FCSTD DOCUMENT  (FreeCAD 1.0R39319 (Git))
Label: Assy_Simulator_Mockup
License: All rights reserved
LicenseURL: https://en.wikipedia.org/wiki/All_rights_reserved
objects: App::AnnotationLabel×5, App::DocumentObjectGroup×4, App::Link×3, PartDesign::CoordinateSystem×1, App::FeaturePython×1, App::Part×1
note: 1 computed .brp shape members not serialized (recipe doc carries the construction recipe); baked Part::Feature solids carry a one-line shape summary decoded from their .brp
EXTERNAL_REF file=../../Part/Misc/Floor.FCStd obj=reference_point
EXTERNAL_REF file=../../Part/Misc/Floor.FCStd obj=Part
EXTERNAL_REF file=Assy_PiTrac.FCStd obj=LCS_Origin
EXTERNAL_REF file=Assy_PiTrac.FCStd obj=Assembly
EXTERNAL_REF file=Assy_Calibration_Rig.FCStd obj=LCS_Origin
EXTERNAL_REF file=Assy_Calibration_Rig.FCStd obj=Assembly

FEATURE [App::DocumentObjectGroup] Parts
FEATURE [PartDesign::CoordinateSystem] LCS_Origin
  AttacherType = Attacher::AttachEngine3D
  AttachmentSupport = -> [X_Axis]
  MapMode = 2
FEATURE [App::DocumentObjectGroup] Constraints
FEATURE [App::FeaturePython] Variables  # WARN: FeaturePython — macro-defined, semantics opaque (R4)
  Type = App::PropertyContainer
FEATURE [App::DocumentObjectGroup] Configurations
FEATURE [App::Link] Floor
  AttachedBy = #reference_point
  AttachedTo = Parent Assembly#LCS_Origin
  LinkedObject = -> <external ../../Part/Misc/Floor.FCStd>#Part
  SolverId = Asm4EE
  expr: Placement = LCS_Origin.Placement * AttachmentOffset * Floor#reference_point.Placement ^ -1
FEATURE [App::Link] Assy_PiTrac
  AttachedBy = #LCS_Origin
  AttachedTo = Floor#reference_point
  AttachmentOffset = pos=(-66.5,5,16.5) rot=(0,0,1;0rad)
  LinkPlacement = pos=(-66.5,5,16.5) rot=(0,0,1;0rad)
  LinkedObject = -> <external Assy_PiTrac.FCStd>#Assembly
  Placement = pos=(-66.5,5,16.5) rot=(0,0,1;0rad)
  SolverId = Asm4EE
  expr: Placement = Floor.Placement * Floor#reference_point.Placement * AttachmentOffset * Assy_PiTrac#LCS_Origin.Placement ^ -1
FEATURE [App::Link] Assy_Calibration_Rig
  AttachedBy = #LCS_Origin
  AttachedTo = Parent Assembly#LCS_Origin
  AttachmentOffset = pos=(-521.5,0,-432.5) rot=(0,0,1;0rad)
  LinkPlacement = pos=(-521.5,0,-432.5) rot=(0,0,1;0rad)
  LinkedObject = -> <external Assy_Calibration_Rig.FCStd>#Assembly
  Placement = pos=(-521.5,0,-432.5) rot=(0,0,1;0rad)
  SolverId = Asm4EE
  expr: Placement = LCS_Origin.Placement * AttachmentOffset * Assy_Calibration_Rig#LCS_Origin.Placement ^ -1
FEATURE [App::Part] Assembly  label="Assy_Simulator_Mockup"
  AssemblyType = Part::Link
  Group = -> [LCS_Origin,Constraints,Variables,Configurations,Floor,Assy_PiTrac,Assy_Calibration_Rig]
  Origin = -> Origin
  Type = Assembly
FEATURE [App::AnnotationLabel] MeasureLbl
  BasePosition = (0,198.805,-422.5)
  LabelText = Coordinates : | X : 0.000 | Y : 198.805 | Z : -422.499
  TextPosition = (335.894,31.99,-0.000305176)
FEATURE [App::AnnotationLabel] MeasureLbl001
  BasePosition = (-116.5,21.335,-432.5)
  LabelText = Coordinates : | X : -116.499 | Y : 21.335 | Z : -432.499
  TextPosition = (455.348,-114.954,0.000762939)
FEATURE [App::AnnotationLabel] MeasureLbl002
  BasePosition = (-521.5,21.335,-432.5)
  LabelText = Coordinates : | X : -521.499 | Y : 21.335 | Z : -432.499
  TextPosition = (-293.353,96.2344,0)
FEATURE [App::AnnotationLabel] MeasureLbl003
  BasePosition = (-4.97e-14,265,50)
  LabelText = Coordinates : | X : 0.000 | Y : 265.000 | Z : 50.000
  TextPosition = (0,0,300)
FEATURE [App::AnnotationLabel] MeasureLbl004
  BasePosition = (-2.13e-14,90,50)
  LabelText = Coordinates : | X : 0.000 | Y : 90.000 | Z : 50.000
  TextPosition = (0,0,300)
FEATURE [App::DocumentObjectGroup] Measures
  Group = -> [MeasureLbl,MeasureLbl001,MeasureLbl002,MeasureLbl003,MeasureLbl004]

RESOLVED EXTERNAL PARTS (link-assembly join: the EXTERNAL_REF files above that resolve inside this repo's crawl, each included once):
---- part ../../Part/Misc/Floor.FCStd = doc fcstd_6bb5dbe66d4c ----
FCSTD DOCUMENT  (FreeCAD 1.0R39319 (Git))
Label: Floor
License: All rights reserved
LicenseURL: https://en.wikipedia.org/wiki/All_rights_reserved
objects: PartDesign::CoordinateSystem×3, Sketcher::SketchObject×1, PartDesign::Pad×1, PartDesign::Body×1, App::Part×1
note: 9 computed .brp shape members not serialized (recipe doc carries the construction recipe); baked Part::Feature solids carry a one-line shape summary decoded from their .brp

FEATURE [Sketcher::SketchObject] Sketch
  ArcFitTolerance = 1e-06
  AttachmentSupport = -> [XZ_Plane001]
  FullyConstrained = false
  MakeInternals = false
  MapMode = 5
  Placement = pos=(0,0,0) rot=(1,0,0;1.5708rad)
  sketch-geometry (4):
    g0: LineSegment StartX=-999.904 StartY=500 StartZ=0 EndX=-1000.1 EndY=-1500 EndZ=0
    g1: LineSegment StartX=-1000.1 StartY=-1500 StartZ=0 EndX=999.904 EndY=-1500 EndZ=0
    g2: LineSegment StartX=999.904 StartY=-1500 StartZ=0 EndX=999.904 EndY=500 EndZ=0
    g3: LineSegment StartX=999.904 StartY=500 StartZ=0 EndX=-999.904 EndY=500 EndZ=0
  constraints (10):
    c: Coincident(g0,g1)
    c: Coincident(g1,g2)
    c: Coincident(g2,g3)
    c: Coincident(g3,g0)
    c: Vertical(g2)
    c: Horizontal(g1)
    c: Distance(g2,g0) = 2000
    c: Distance(g1,g3) = 2000
    c: Symmetric(g0,g2,g-2)
    c: Distance(g3,g-1) = 500
FEATURE [PartDesign::Pad] Pad
  Direction = (0,-1,2e-16)
  Length = 10
  Length2 = 10
  Placement = pos=(0,0,0) rot=(1,0,0;1.5708rad)
  Profile = -> Sketch
  ReferenceAxis = -> Sketch [N_Axis]
  Refine = true
  Suppressed = false
  Type = 0
FEATURE [PartDesign::Body] Body  label="Floor001"
  AllowCompound = false
  Group = -> [Sketch,Pad]
  Origin = -> Origin001
  Tip = -> Pad
FEATURE [PartDesign::CoordinateSystem] reference_point  label="reference point"
  AttacherType = Attacher::AttachEngine3D
FEATURE [PartDesign::CoordinateSystem] ball_flight  label="ball flight"
  AttacherType = Attacher::AttachEngine3D
  AttachmentOffset = pos=(0,177.25,-422.25) rot=(0,0,1;0rad)
  AttachmentSupport = -> [XY_Plane]
  MapMode = 5
  Placement = pos=(0,177.25,-422.25) rot=(0,0,1;0rad)
FEATURE [PartDesign::CoordinateSystem] ball_tee_back  label="ball tee back"
  AttacherType = Attacher::AttachEngine3D
  AttachmentOffset = pos=(-522.75,0,-431.25) rot=(0,0,1;0rad)
  AttachmentSupport = -> [XY_Plane]
  MapMode = 5
  Placement = pos=(-522.75,0,-431.25) rot=(0,0,1;0rad)
FEATURE [App::Part] Part  label="Floor"
  Group = -> [Body,reference_point,ball_flight,ball_tee_back]
  Origin = -> Origin
---- part Assy_PiTrac.FCStd = doc fcstd_6580bbd02c6c ----
FCSTD DOCUMENT  (FreeCAD 1.0R39319 (Git))
Label: Assy_PiTrac
License: All rights reserved
LicenseURL: https://en.wikipedia.org/wiki/All_rights_reserved
objects: TechDraw::DrawViewBalloon×30, App::Link×9, TechDraw::DrawProjGroupItem×6, TechDraw::DrawViewDimension×6, App::DocumentObjectGroup×3, TechDraw::DrawSVGTemplate×2, TechDraw::DrawViewSection×2, TechDraw::DrawViewAnnotation×2, TechDraw::DrawPage×2, PartDesign::CoordinateSystem×1, App::FeaturePython×1, App::Part×1, Spreadsheet::Sheet×1, TechDraw::DrawProjGroup×1, TechDraw::DrawViewSpreadsheet×1, TechDraw::DrawViewDimExtent×1
note: 15 computed .brp shape members not serialized (recipe doc carries the construction recipe); baked Part::Feature solids carry a one-line shape summary decoded from their .brp
EXTERNAL_REF file=Assy_Stack_Module_PSU.FCStd obj=LCS_Origin
EXTERNAL_REF file=Assy_Stack_Module_PSU.FCStd obj=Assembly
EXTERNAL_REF file=Assy_Stack_Module_Flight_Cam.FCStd obj=LCS_Origin
EXTERNAL_REF file=Assy_Stack_Module_Flight_Cam.FCStd obj=Assembly
EXTERNAL_REF file=Assy_Stack_Module_LED.FCStd obj=LCS_Origin
EXTERNAL_REF file=Assy_Stack_Module_LED.FCStd obj=Assembly
EXTERNAL_REF file=Assy_Stack_Module_Tee_Cam.FCStd obj=LCS_Origin
EXTERNAL_REF file=Assy_Stack_Module_Tee_Cam.FCStd obj=Assembly
EXTERNAL_REF file=Assy_Stack_Module_Cover_forInserts.FCStd obj=LCS_Origin
EXTERNAL_REF file=Assy_Stack_Module_Cover_forInserts.FCStd obj=Assembly
EXTERNAL_REF file=Assy_RaspberryPi5_carrier.FCStd obj=LCS_Origin
EXTERNAL_REF file=Assy_RaspberryPi5_carrier.FCStd obj=Assembly
EXTERNAL_REF file=Assy_V3Connector_Board.FCStd obj=LCS_Origin
EXTERNAL_REF file=Assy_V3Connector_Board.FCStd obj=Assembly
EXTERNAL_REF file=../../Part/Purchase/Acrylic_Backplate.FCStd obj=LCS_1
EXTERNAL_REF file=../../Part/Purchase/Acrylic_Backplate.FCStd obj=Part
EXTERNAL_REF file=../../Part/Purchase/Shank_Shield.FCStd obj=LCS_1
EXTERNAL_REF file=../../Part/Purchase/Shank_Shield.FCStd obj=Part

FEATURE [App::DocumentObjectGroup] Parts
FEATURE [PartDesign::CoordinateSystem] LCS_Origin
  AttacherType = Attacher::AttachEngine3D
  AttachmentSupport = -> [X_Axis]
  MapMode = 2
FEATURE [App::DocumentObjectGroup] Constraints
FEATURE [App::FeaturePython] Variables  # WARN: FeaturePython — macro-defined, semantics opaque (R4)
  Type = App::PropertyContainer
FEATURE [App::DocumentObjectGroup] Configurations
FEATURE [App::Link] Assy_Stack_Module_PSU
  AttachedBy = #LCS_Origin
  AttachedTo = Parent Assembly#LCS_Origin
  LinkedObject = -> <external Assy_Stack_Module_PSU.FCStd>#Assembly
  SolverId = Asm4EE
  expr: Placement = LCS_Origin.Placement * AttachmentOffset * Assy_Stack_Module_PSU#LCS_Origin.Placement ^ -1
FEATURE [App::Link] Assy_Stack_Module_Flight_Cam
  AttachedBy = #LCS_Origin
  AttachedTo = Assy_Stack_Module_PSU#LCS_Origin
  AttachmentOffset = pos=(116.5,43.25,33.5) rot=(-0.57735,0.57735,-0.57735;4.18879rad)
  LinkPlacement = pos=(116.5,43.25,33.5) rot=(-0.57735,0.57735,-0.57735;4.18879rad)
  LinkedObject = -> <external Assy_Stack_Module_Flight_Cam.FCStd>#Assembly
  Placement = pos=(116.5,43.25,33.5) rot=(-0.57735,0.57735,-0.57735;4.18879rad)
  SolverId = Asm4EE
  expr: Placement = Assy_Stack_Module_PSU.Placement * Assy_Stack_Module_PSU#LCS_Origin.Placement * AttachmentOffset * Assy_Stack_Module_Flight_Cam#LCS_Origin.Placement ^ -1
FEATURE [App::Link] Assy_Stack_Module_LED
  AttachedBy = #LCS_Origin
  AttachedTo = Assy_Stack_Module_Flight_Cam#LCS_Origin
  AttachmentOffset = pos=(0,0,-87.5) rot=(0,0,1;0rad)
  LinkPlacement = pos=(116.5,130.75,33.5) rot=(-0.57735,0.57735,-0.57735;4.18879rad)
  LinkedObject = -> <external Assy_Stack_Module_LED.FCStd>#Assembly
  Placement = pos=(116.5,130.75,33.5) rot=(-0.57735,0.57735,-0.57735;4.18879rad)
  SolverId = Asm4EE
  expr: Placement = Assy_Stack_Module_Flight_Cam.Placement * Assy_Stack_Module_Flight_Cam#LCS_Origin.Placement * AttachmentOffset * Assy_Stack_Module_LED#LCS_Origin.Placement ^ -1
FEATURE [App::Link] Assy_Stack_Module_Tee_Cam
  AttachedBy = #LCS_Origin
  AttachedTo = Assy_Stack_Module_LED#LCS_Origin
  AttachmentOffset = pos=(0,0,-87.5) rot=(0,0,1;0rad)
  LinkPlacement = pos=(116.5,218.25,33.5) rot=(-0.57735,0.57735,-0.57735;4.18879rad)
  LinkedObject = -> <external Assy_Stack_Module_Tee_Cam.FCStd>#Assembly
  Placement = pos=(116.5,218.25,33.5) rot=(-0.57735,0.57735,-0.57735;4.18879rad)
  SolverId = Asm4EE
  expr: Placement = Assy_Stack_Module_LED.Placement * Assy_Stack_Module_LED#LCS_Origin.Placement * AttachmentOffset * Assy_Stack_Module_Tee_Cam#LCS_Origin.Placement ^ -1
FEATURE [App::Link] Assy_Stack_Module_Cover_forInserts
  AttachedBy = #LCS_Origin
  AttachedTo = Assy_Stack_Module_Tee_Cam#LCS_Origin
  AttachmentOffset = pos=(82.5,-13.5,-84.5) rot=(0.57735,-0.57735,0.57735;2.0944rad)
  LinkPlacement = pos=(130,302.75,116) rot=(-0.57735,0.57735,-0.57735;2.0944rad)
  LinkedObject = -> <external Assy_Stack_Module_Cover_forInserts.FCStd>#Assembly
  Placement = pos=(130,302.75,116) rot=(-0.57735,0.57735,-0.57735;2.0944rad)
  SolverId = Asm4EE
  expr: Placement = Assy_Stack_Module_Tee_Cam.Placement * Assy_Stack_Module_Tee_Cam#LCS_Origin.Placement * AttachmentOffset * Assy_Stack_Module_Cover_forInserts#LCS_Origin.Placement ^ -1
FEATURE [App::Link] Assy_RaspberryPi5_carrier
  AttachedBy = #LCS_Origin
  AttachedTo = Assy_Stack_Module_Tee_Cam#LCS_Origin
  AttachmentOffset = pos=(45,105,-38.5) rot=(0.57735,-0.57735,0.57735;4.18879rad)
  LinkPlacement = pos=(11.5,256.75,78.5) rot=(0,0,1;0rad)
  LinkedObject = -> <external Assy_RaspberryPi5_carrier.FCStd>#Assembly
  Placement = pos=(11.5,256.75,78.5) rot=(0,0,1;0rad)
  SolverId = Asm4EE
  expr: Placement = Assy_Stack_Module_Tee_Cam.Placement * Assy_Stack_Module_Tee_Cam#LCS_Origin.Placement * AttachmentOffset * Assy_RaspberryPi5_carrier#LCS_Origin.Placement ^ -1
FEATURE [App::Link] Assy_V3Connector_Board
  AttachedBy = #LCS_Origin
  AttachedTo = Assy_Stack_Module_Flight_Cam#LCS_Origin
  AttachmentOffset = pos=(52,50,-55) rot=(0.707107,-0.707107,0;3.14159rad)
  LinkPlacement = pos=(66.5,98.25,85.5) rot=(-1,0,0;1.5708rad)
  LinkedObject = -> <external Assy_V3Connector_Board.FCStd>#Assembly
  Placement = pos=(66.5,98.25,85.5) rot=(-1,0,0;1.5708rad)
  SolverId = Asm4EE
  expr: Placement = Assy_Stack_Module_Flight_Cam.Placement * Assy_Stack_Module_Flight_Cam#LCS_Origin.Placement * AttachmentOffset * Assy_V3Connector_Board#LCS_Origin.Placement ^ -1
FEATURE [App::Link] Acrylic_Backplate
  AttachedBy = #LCS_1
  AttachedTo = Parent Assembly#LCS_Origin
  AttachmentOffset = pos=(11,37,117) rot=(0,0,1;0rad)
  LinkPlacement = pos=(11,37,117) rot=(0,0,1;0rad)
  LinkedObject = -> <external ../../Part/Purchase/Acrylic_Backplate.FCStd>#Part
  Placement = pos=(11,37,117) rot=(0,0,1;0rad)
  SolverId = Asm4EE
  expr: Placement = LCS_Origin.Placement * AttachmentOffset * Acrylic_Backplate#LCS_1.Placement ^ -1
FEATURE [App::Link] Shank_Shield
  AttachedBy = #LCS_1
  AttachedTo = Parent Assembly#LCS_Origin
  AttachmentOffset = pos=(-3,40,-13) rot=(0,0,1;0rad)
  LinkPlacement = pos=(-3,40,-13) rot=(0,0,1;0rad)
  LinkedObject = -> <external ../../Part/Purchase/Shank_Shield.FCStd>#Part
  Placement = pos=(-3,40,-13) rot=(0,0,1;0rad)
  SolverId = Asm4EE
  expr: Placement = LCS_Origin.Placement * AttachmentOffset * Shank_Shield#LCS_1.Placement ^ -1
FEATURE [App::Part] Assembly  label="Assy_PiTrac"
  AssemblyType = Part::Link
  Group = -> [LCS_Origin,Constraints,Variables,Configurations,Assy_Stack_Module_PSU,Assy_Stack_Module_Flight_Cam,Assy_Stack_Module_LED,Assy_Stack_Module_Tee_Cam,Assy_Stack_Module_Cover_forInserts,Assy_RaspberryPi5_carrier,Assy_V3Connector_Board,Acrylic_Backplate,Shank_Shield]
  Origin = -> Origin
  Type = Assembly
FEATURE [Spreadsheet::Sheet] Spreadsheet  label="BOM"
  cells = A1=16; B1=1; C1='Acrylic Backplate; A2=15; B2=1; C2='Acrylic Shankshield; A3=14; B3=4; C3='M5x306 mm rod; D3==306 mm; A4=13; B4=4; C4='M5 x 12 mm sleeve nut; A5=12; B5=4; C5='ISO 7380-2 M5x10 mm screw; D5='10 mm; ISO 4762 optional; A6=11; B6=12; C6='ISO 7380-2 M5x15 mm screw; D6='10–15 mm; ISO 4762 optional; A7=10; B7=4; C7='ISO 10511 M5 lock nut; A8=9; B8=4; C8='ISO 4032 M5 nut; A9=8; B9=4; C9='Foot; E9='PETG or PLA; A10=7; B10=4; C10='Carrier_Clamps; E10='PETG or PLA; A11=6; B11=1; C11='Pi 5 Assembly; A12=5; B12=1; C12='ConnectorBoardv3 Assembly; A13=4; B13=1; C13='Stack Module Cover Assembly; A14=3; B14=1; C14='PSU Stack Module Assembly; D14='-; A15=2; B15=1; C15='LED Stack Module Assembly; D15='-; A16=1; B16=2; C16='Camera Stack Module Assembly; D16='-; A17='Position; B17='Quantity; C17='Part; D17='Dimensions; E17='Material
FEATURE [TechDraw::DrawSVGTemplate] Template
  EditableTexts = approval_person=GitHub PR; creator=Stefan; date_of_issue=20.03.2026; document_type=Assembly Drawing; general_tolerances=na; identification_number=na; language_code=EN; part_material=na; revision_index=AAA; scale=1 : 1; sheet_number=1 / 1; title=Assy_PiTrac
  Height = 594
  Orientation = 1
  Template = <userpath>/Documents/PiTrac/3D Printed Parts/Enclosure Version 3/Assets/PiTrac_A1_Landscape_ISO5457_minimal.svg
  Width = 841
FEATURE [TechDraw::DrawProjGroupItem] View
  CoarseView = false
  Direction = (-0.57735,0.57735,-0.57735)
  Focus = 100
  HardHidden = false
  IsoCount = 0
  IsoHidden = false
  IsoVisible = false
  LockPosition = false
  Perspective = false
  Rotation = 0
  RotationVector = (1,0,0)
  Scale = 0.5
  ScaleType = 2
  ScrubCount = 1
  SeamHidden = false
  SeamVisible = false
  SmoothHidden = false
  SmoothVisible = true
  Source = -> [Assembly]
  Type = 0
  X = 552.509
  XDirection = (-0.707106,0,0.707106)
  Y = 140.759
FEATURE [TechDraw::DrawProjGroupItem] View001  label="Front"
  CoarseView = false
  Direction = (0,0,-1)
  Focus = 100
  HardHidden = false
  IsoCount = 0
  IsoHidden = false
  IsoVisible = false
  LockPosition = true
  Perspective = false
  Rotation = 0
  RotationVector = (1,0,0)
  Scale = 0.5
  ScaleType = 2
  ScrubCount = 1
  SeamHidden = false
  SeamVisible = false
  SmoothHidden = false
  SmoothVisible = true
  Source = -> [Assembly]
  Type = 0
  X = 0
  XDirection = (-1,0,0)
  Y = 0
FEATURE [TechDraw::DrawProjGroupItem] ProjItem  label="Left"
  CoarseView = false
  Direction = (1,0,-1e-16)
  Focus = 100
  HardHidden = false
  IsoCount = 0
  IsoHidden = false
  IsoVisible = false
  LockPosition = false
  Perspective = false
  Rotation = 0
  RotationVector = (1,0,0)
  Scale = 0.5
  ScaleType = 2
  ScrubCount = 1
  SeamHidden = false
  SeamVisible = false
  SmoothHidden = false
  SmoothVisible = true
  Source = -> [Assembly]
  Type = 1
  X = 101
  XDirection = (-1e-16,0,-1)
  Y = 0
FEATURE [TechDraw::DrawProjGroupItem] ProjItem001  label="Rear"
  CoarseView = false
  Direction = (0,0,1)
  Focus = 100
  HardHidden = false
  IsoCount = 0
  IsoHidden = false
  IsoVisible = false
  LockPosition = false
  Perspective = false
  Rotation = 0
  RotationVector = (1,0,0)
  Scale = 0.5
  ScaleType = 2
  ScrubCount = 1
  SeamHidden = false
  SeamVisible = false
  SmoothHidden = false
  SmoothVisible = true
  Source = -> [Assembly]
  Type = 3
  X = 202
  XDirection = (1,0,0)
  Y = 0
FEATURE [TechDraw::DrawProjGroupItem] ProjItem002  label="Top"
  CoarseView = false
  Direction = (0,1,0)
  Focus = 100
  HardHidden = false
  IsoCount = 0
  IsoHidden = false
  IsoVisible = false
  LockPosition = false
  Perspective = false
  Rotation = 0
  RotationVector = (1,0,0)
  Scale = 0.5
  ScaleType = 2
  ScrubCount = 1
  SeamHidden = false
  SeamVisible = false
  SmoothHidden = false
  SmoothVisible = true
  Source = -> [Assembly]
  Type = 4
  X = 0
  XDirection = (-1,0,0)
  Y = -146.779
FEATURE [TechDraw::DrawProjGroup] ProjGroup
  Anchor = -> View001
  AutoDistribute = true
  LockPosition = false
  ProjectionType = 0
  Rotation = 0
  Scale = 0.5
  ScaleType = 2
  Source = -> [Assembly]
  Views = -> [View001,ProjItem,ProjItem001,ProjItem002]
  X = 169.846
  Y = 386.4
  spacingX = 15
  spacingY = 15
FEATURE [TechDraw::DrawViewSection] SectionView  label="Section A - A"
  BaseView = -> View001
  CoarseView = false
  CutSurfaceDisplay = 2
  Direction = (1,-1e-16,0)
  FileGeomPattern = <path>\data\Mod/TechDraw/PAT/FCPAT.pat
  FileHatchPattern = <path>\data\Mod/TechDraw/Patterns/simple.svg
  Focus = 100
  FuseBeforeCut = false
  HardHidden = false
  HatchOffset = (0,0,0)
  HatchRotation = 0
  HatchScale = 1
  IsoCount = 0
  IsoHidden = false
  IsoVisible = false
  LockPosition = false
  NameGeomPattern = Diamond
  Perspective = false
  Rotation = -90
  Scale = 0.5
  ScaleType = 2
  ScrubCount = 1
  SeamHidden = false
  SeamVisible = false
  SectionDirection = 4
  SectionLineStretch = 1
  SectionNormal = (1,-1e-16,0)
  SectionOrigin = (66.5,164.89,48.5)
  SectionSymbol = A
  SmoothHidden = false
  SmoothVisible = true
  Source = -> [Assembly]
  TrimAfterCut = false
  UsePreviousCut = false
  X = 505.075
  XDirection = (-1e-16,-1,0)
  Y = 347.597
FEATURE [TechDraw::DrawViewSection] SectionView001  label="Section B - B"
  BaseView = -> View001
  CoarseView = false
  CutSurfaceDisplay = 2
  Direction = (1,-1e-16,0)
  FileGeomPattern = <path>\data\Mod/TechDraw/PAT/FCPAT.pat
  FileHatchPattern = <path>\data\Mod/TechDraw/Patterns/simple.svg
  Focus = 100
  FuseBeforeCut = false
  HardHidden = false
  HatchOffset = (0,0,0)
  HatchRotation = 0
  HatchScale = 1
  IsoCount = 0
  IsoHidden = false
  IsoVisible = false
  LockPosition = false
  NameGeomPattern = Diamond
  Perspective = false
  Rotation = -90
  Scale = 0.5
  ScaleType = 2
  ScrubCount = 1
  SeamHidden = false
  SeamVisible = false
  SectionDirection = 4
  SectionLineStretch = 1
  SectionNormal = (1,-1e-16,0)
  SectionOrigin = (0,164.89,48.5)
  SectionSymbol = B
  SmoothHidden = false
  SmoothVisible = true
  Source = -> [Assembly]
  TrimAfterCut = false
  UsePreviousCut = false
  X = 634.219
  XDirection = (-1e-16,-1,0)
  Y = 350.177
FEATURE [TechDraw::DrawViewSpreadsheet] Sheet
  CellEnd = E17
  CellStart = A1
  Font = osifont
  LineWidth = 0.35
  LockPosition = false
  Rotation = 0
  ScaleType = 2
  Source = -> Spreadsheet
  Symbol = <blob: 18577 chars omitted>
  TextSize = 12
  X = 730.475
  Y = 140.759
FEATURE [TechDraw::DrawViewBalloon] Balloon
  BubbleShape = 0
  EndType = 0
  EndTypeScale = 1
  KinkLength = 5
  LockPosition = false
  OriginX = -53.9464
  OriginY = -116.086
  Rotation = 0
  ScaleType = 0
  ShapeScale = 1
  SourceView = -> View001
  Text = 1
  TextWrapLen = -1
  X = -105
  Y = -87.7835
FEATURE [TechDraw::DrawViewBalloon] Balloon001
  BubbleShape = 0
  EndType = 0
  EndTypeScale = 1
  KinkLength = 5
  LockPosition = false
  OriginX = -57.2885
  OriginY = 56.0294
  Rotation = 0
  ScaleType = 0
  ShapeScale = 1
  SourceView = -> View001
  Text = 1
  TextWrapLen = -1
  X = -105
  Y = 91.0163
FEATURE [TechDraw::DrawViewBalloon] Balloon002
  BubbleShape = 0
  EndType = 0
  EndTypeScale = 1
  KinkLength = 5
  LockPosition = false
  OriginX = -55.6174
  OriginY = -29.193
  Rotation = 0
  ScaleType = 0
  ShapeScale = 1
  SourceView = -> View001
  Text = 2
  TextWrapLen = -1
  X = -105
  Y = 10.807
FEATURE [TechDraw::DrawViewBalloon] Balloon003
  BubbleShape = 0
  EndType = 0
  EndTypeScale = 1
  KinkLength = 5
  LockPosition = false
  OriginX = -67.3146
  OriginY = -156.191
  Rotation = 0
  ScaleType = 0
  ShapeScale = 1
  SourceView = -> View001
  Text = 3
  TextWrapLen = -1
  X = -105
  Y = -116.191
FEATURE [TechDraw::DrawViewBalloon] Balloon004
  BubbleShape = 0
  EndType = 0
  EndTypeScale = 1
  KinkLength = 5
  LockPosition = false
  OriginX = -58.9595
  OriginY = 142.923
  Rotation = 0
  ScaleType = 0
  ShapeScale = 1
  SourceView = -> View001
  Text = 4
  TextWrapLen = -1
  X = -105
  Y = 150.136
FEATURE [TechDraw::DrawViewBalloon] Balloon005
  BubbleShape = 0
  EndType = 0
  EndTypeScale = 1
  KinkLength = 5
  LockPosition = false
  OriginX = 21.6383
  OriginY = -60.9425
  Rotation = 0
  ScaleType = 0
  ShapeScale = 1
  SourceView = -> ProjItem001
  Text = 5
  TextWrapLen = -1
  X = 105
  Y = -82.7705
FEATURE [TechDraw::DrawViewBalloon] Balloon006
  BubbleShape = 0
  EndType = 0
  EndTypeScale = 1
  KinkLength = 5
  LockPosition = false
  OriginX = 19.9672
  OriginY = 84.4368
  Rotation = 0
  ScaleType = 0
  ShapeScale = 1
  SourceView = -> ProjItem001
  Text = 6
  TextWrapLen = -1
  X = 105
  Y = 92.6873
FEATURE [TechDraw::DrawViewBalloon] Balloon007
  BubbleShape = 0
  EndType = 0
  EndTypeScale = 1
  KinkLength = 5
  LockPosition = false
  OriginX = 63.5
  OriginY = -169.885
  Rotation = 0
  ScaleType = 0
  ShapeScale = 1
  SourceView = -> ProjItem001
  Text = 8
  TextWrapLen = -1
  X = 60.7895
  Y = -220
FEATURE [TechDraw::DrawViewBalloon] Balloon008
  BubbleShape = 0
  EndType = 0
  EndTypeScale = 1
  KinkLength = 5
  LockPosition = false
  OriginX = -63.5
  OriginY = -169.885
  Rotation = 0
  ScaleType = 0
  ShapeScale = 1
  SourceView = -> ProjItem001
  Text = 8
  TextWrapLen = -1
  X = -23.5
  Y = -220
FEATURE [TechDraw::DrawViewBalloon] Balloon009
  BubbleShape = 0
  EndType = 0
  EndTypeScale = 1
  KinkLength = 5
  LockPosition = false
  OriginX = 153.721
  OriginY = 42.0732
  Rotation = 0
  ScaleType = 0
  ShapeScale = 1
  SourceView = -> SectionView001
  Text = 9
  TextWrapLen = -1
  X = 175
  Y = -110
FEATURE [TechDraw::DrawViewAnnotation] Annotation001
  Font = osifont
  LineSpace = 100
  LockPosition = false
  MaxWidth = -1
  Rotation = 0
  ScaleType = 0
  Text = glue into feet
  TextSize = 5
  TextStyle = 0
  X = 752.988
  Y = 294.799
FEATURE [TechDraw::DrawViewBalloon] Balloon010
  BubbleShape = 0
  EndType = 0
  EndTypeScale = 1
  KinkLength = 5
  LockPosition = false
  OriginX = 146.418
  OriginY = 42.9281
  Rotation = 0
  ScaleType = 0
  ShapeScale = 1
  SourceView = -> SectionView001
  Text = 10
  TextWrapLen = -1
  X = 175
  Y = -77.2267
FEATURE [TechDraw::DrawViewBalloon] Balloon011
  BubbleShape = 0
  EndType = 0
  EndTypeScale = 1
  KinkLength = 5
  LockPosition = false
  OriginX = -58.0981
  OriginY = 47.677
  Rotation = 0
  ScaleType = 0
  ShapeScale = 1
  SourceView = -> SectionView
  Text = 11
  TextWrapLen = -1
  X = 110
  Y = 79.3081
FEATURE [TechDraw::DrawViewBalloon] Balloon012
  BubbleShape = 0
  EndType = 0
  EndTypeScale = 1
  KinkLength = 5
  LockPosition = false
  OriginX = 24.4992
  OriginY = -14.3372
  Rotation = 0
  ScaleType = 0
  ShapeScale = 1
  SourceView = -> Balloon011
  Text = 11
  TextWrapLen = -1
  X = 55
  Y = 0.377126
FEATURE [TechDraw::DrawViewBalloon] Balloon013
  BubbleShape = 0
  EndType = 0
  EndTypeScale = 1
  KinkLength = 5
  LockPosition = false
  OriginX = -58.5385
  OriginY = -24.6701
  Rotation = 0
  ScaleType = 0
  ShapeScale = 1
  SourceView = -> SectionView
  Text = 11
  TextWrapLen = -1
  X = -110
  Y = 77.5462
FEATURE [TechDraw::DrawViewBalloon] Balloon014
  BubbleShape = 0
  EndType = 0
  EndTypeScale = 1
  KinkLength = 5
  LockPosition = false
  OriginX = -11.7845
  OriginY = -14.2271
  Rotation = 0
  ScaleType = 0
  ShapeScale = 1
  SourceView = -> Balloon013
  Text = 11
  TextWrapLen = -1
  X = -55
  Y = -1.38475
FEATURE [TechDraw::DrawViewBalloon] Balloon015
  BubbleShape = 0
  EndType = 0
  EndTypeScale = 1
  KinkLength = 5
  LockPosition = false
  OriginX = 115.998
  OriginY = 49.6591
  Rotation = 0
  ScaleType = 0
  ShapeScale = 1
  SourceView = -> SectionView
  Text = 12
  TextWrapLen = -1
  X = 110
  Y = -99.1311
FEATURE [TechDraw::DrawViewBalloon] Balloon016
  BubbleShape = 0
  EndType = 0
  EndTypeScale = 1
  KinkLength = 5
  LockPosition = false
  OriginX = 115.998
  OriginY = -23.0184
  Rotation = 0
  ScaleType = 0
  ShapeScale = 1
  SourceView = -> SectionView
  Text = 12
  TextWrapLen = -1
  X = -110
  Y = -96.4394
FEATURE [TechDraw::DrawViewDimension] Dimension
  AngleOverride = false
  Arbitrary = false
  ArbitraryTolerances = false
  BoxCorners = (2) [(-47.5,-84.9426,-1e-07),(47.5,84.9426,1e-07)]
  EqualTolerance = true
  ExtensionAngle = 0
  FormatSpec = %.2w
  FormatSpecOverTolerance = %+.2w
  FormatSpecUnderTolerance = %+.2w
  Inverted = false
  LineAngle = 0
  LockPosition = false
  MeasureType = 1
  OverTolerance = 0
  References2D = -> [SectionView]
  Rotation = 0
  ScaleType = 0
  TheoreticalExact = false
  Type = 0
  UnderTolerance = 0
  X = 69.7674
  Y = 0.858084
FEATURE [TechDraw::DrawViewDimension] Dimension001
  AngleOverride = false
  Arbitrary = false
  ArbitraryTolerances = false
  BoxCorners = (2) [(-47.5,-84.9426,-1e-07),(47.5,84.9426,1e-07)]
  EqualTolerance = true
  ExtensionAngle = 0
  FormatSpec = %.1w
  FormatSpecOverTolerance = %+.2w
  FormatSpecUnderTolerance = %+.2w
  Inverted = false
  LineAngle = 0
  LockPosition = false
  MeasureType = 1
  OverTolerance = 0
  References2D = -> [SectionView]
  Rotation = 0
  ScaleType = 0
  TheoreticalExact = false
  Type = 0
  UnderTolerance = 0
  X = 61.0108
  Y = 93.6752
FEATURE [TechDraw::DrawViewDimension] Dimension002
  AngleOverride = false
  Arbitrary = false
  ArbitraryTolerances = false
  BoxCorners = (2) [(-47.5,-84.9426,-1e-07),(47.5,84.9426,1e-07)]
  EqualTolerance = true
  ExtensionAngle = 0
  FormatSpec = %.2w
  FormatSpecOverTolerance = %+.2w
  FormatSpecUnderTolerance = %+.2w
  Inverted = false
  LineAngle = 0
  LockPosition = false
  MeasureType = 1
  OverTolerance = 0
  References2D = -> [SectionView]
  Rotation = 0
  ScaleType = 0
  TheoreticalExact = false
  Type = 0
  UnderTolerance = 0
  X = 74.7368
  Y = -60.3801
FEATURE [TechDraw::DrawViewBalloon] Balloon017
  BubbleShape = 0
  EndType = 0
  EndTypeScale = 1
  KinkLength = 5
  LockPosition = false
  OriginX = -67.739
  OriginY = -51.0045
  Rotation = 0
  ScaleType = 0
  ShapeScale = 1
  SourceView = -> ProjItem002
  Text = 13
  TextWrapLen = -1
  X = -105
  Y = -46.4766
FEATURE [TechDraw::DrawViewBalloon] Balloon018
  BubbleShape = 0
  EndType = 0
  EndTypeScale = 1
  KinkLength = 5
  LockPosition = false
  OriginX = -65.2497
  OriginY = 64.7467
  Rotation = 0
  ScaleType = 0
  ShapeScale = 1
  SourceView = -> ProjItem002
  Text = 13
  TextWrapLen = -1
  X = -105
  Y = 76.7424
FEATURE [TechDraw::DrawViewBalloon] Balloon019
  BubbleShape = 0
  EndType = 0
  EndTypeScale = 1
  KinkLength = 5
  LockPosition = false
  OriginX = 68.5487
  OriginY = -49.7599
  Rotation = 0
  ScaleType = 0
  ShapeScale = 1
  SourceView = -> ProjItem002
  Text = 13
  TextWrapLen = -1
  X = 105
  Y = -73.8586
FEATURE [TechDraw::DrawViewBalloon] Balloon020
  BubbleShape = 0
  EndType = 0
  EndTypeScale = 1
  KinkLength = 5
  LockPosition = false
  OriginX = 65.4371
  OriginY = 64.7467
  Rotation = 0
  ScaleType = 0
  ShapeScale = 1
  SourceView = -> ProjItem002
  Text = 13
  TextWrapLen = -1
  X = 105
  Y = 40.6479
FEATURE [TechDraw::DrawViewBalloon] Balloon021
  BubbleShape = 0
  EndType = 0
  EndTypeScale = 1
  KinkLength = 5
  LockPosition = false
  OriginX = -50.9364
  OriginY = -44.159
  Rotation = 0
  ScaleType = 0
  ShapeScale = 1
  SourceView = -> ProjItem002
  Text = 11
  TextWrapLen = -1
  X = -105
  Y = -7.27059
FEATURE [TechDraw::DrawViewBalloon] Balloon022
  BubbleShape = 0
  EndType = 0
  EndTypeScale = 1
  KinkLength = 5
  LockPosition = false
  OriginX = -50.3141
  OriginY = 23.6737
  Rotation = 0
  ScaleType = 0
  ShapeScale = 1
  SourceView = -> ProjItem002
  Text = 11
  TextWrapLen = -1
  X = -105
  Y = 43.1372
FEATURE [TechDraw::DrawViewBalloon] Balloon023
  BubbleShape = 0
  EndType = 0
  EndTypeScale = 1
  KinkLength = 5
  LockPosition = false
  OriginX = 52.9908
  OriginY = -44.159
  Rotation = 0
  ScaleType = 0
  ShapeScale = 1
  SourceView = -> ProjItem002
  Text = 11
  TextWrapLen = -1
  X = 105
  Y = -20.3393
FEATURE [TechDraw::DrawViewBalloon] Balloon024
  BubbleShape = 0
  EndType = 0
  EndTypeScale = 1
  KinkLength = 5
  LockPosition = false
  OriginX = 54.8577
  OriginY = 23.0514
  Rotation = 0
  ScaleType = 0
  ShapeScale = 1
  SourceView = -> ProjItem002
  Text = 11
  TextWrapLen = -1
  X = 105
  Y = 10.7766
FEATURE [TechDraw::DrawViewDimension] Dimension003
  AngleOverride = false
  Arbitrary = false
  ArbitraryTolerances = false
  BoxCorners = (2) [(-38.5,-47.5,-1e-07),(38.5,47.5,1e-07)]
  EqualTolerance = true
  ExtensionAngle = 0
  FormatSpec = %.2w
  FormatSpecOverTolerance = %+.2w
  FormatSpecUnderTolerance = %+.2w
  Inverted = false
  LineAngle = 0
  LockPosition = false
  MeasureType = 1
  OverTolerance = 0
  References2D = -> [ProjItem002]
  Rotation = 0
  ScaleType = 0
  TheoreticalExact = false
  Type = 0
  UnderTolerance = 0
  X = 0
  Y = -81.0134
FEATURE [TechDraw::DrawViewDimension] Dimension004
  AngleOverride = false
  Arbitrary = false
  ArbitraryTolerances = false
  BoxCorners = (2) [(-38.5,-47.5,-1e-07),(38.5,47.5,1e-07)]
  EqualTolerance = true
  ExtensionAngle = 0
  FormatSpec = %.2w
  FormatSpecOverTolerance = %+.2w
  FormatSpecUnderTolerance = %+.2w
  Inverted = false
  LineAngle = 0
  LockPosition = false
  MeasureType = 1
  OverTolerance = 0
  References2D = -> [ProjItem002]
  Rotation = 0
  ScaleType = 0
  TheoreticalExact = false
  Type = 0
  UnderTolerance = 0
  X = -71.7831
  Y = -4.16176
FEATURE [TechDraw::DrawViewBalloon] Balloon025
  BubbleShape = 0
  EndType = 0
  EndTypeScale = 1
  KinkLength = 5
  LockPosition = false
  OriginX = 84.8806
  OriginY = 37.8072
  Rotation = 0
  ScaleType = 0
  ShapeScale = 1
  SourceView = -> SectionView001
  Text = 14
  TextWrapLen = -1
  X = 175
  Y = -27.9869
FEATURE [TechDraw::DrawViewBalloon] Balloon026
  BubbleShape = 0
  EndType = 0
  EndTypeScale = 1
  KinkLength = 5
  LockPosition = false
  OriginX = -117.553
  OriginY = 58.3706
  Rotation = 0
  ScaleType = 0
  ShapeScale = 1
  SourceView = -> SectionView
  Text = 15
  TextWrapLen = -1
  X = 110
  Y = 135.087
FEATURE [TechDraw::DrawViewBalloon] Balloon027
  BubbleShape = 0
  EndType = 0
  EndTypeScale = 1
  KinkLength = 5
  LockPosition = false
  OriginX = -120.043
  OriginY = -72.3162
  Rotation = 0
  ScaleType = 0
  ShapeScale = 1
  SourceView = -> SectionView
  Text = 16
  TextWrapLen = -1
  X = -110
  Y = 120.774
FEATURE [TechDraw::DrawViewBalloon] Balloon028
  BubbleShape = 0
  EndType = 0
  EndTypeScale = 1
  KinkLength = 5
  LockPosition = false
  OriginX = -111.459
  OriginY = -9.05598
  Rotation = 0
  ScaleType = 0
  ShapeScale = 1
  SourceView = -> Balloon027
  Text = 7
  TextWrapLen = -1
  X = -80.2568
  Y = -20.7942
FEATURE [TechDraw::DrawViewBalloon] Balloon029
  BubbleShape = 0
  EndType = 0
  EndTypeScale = 1
  KinkLength = 5
  LockPosition = false
  OriginX = 8.69063
  OriginY = -35.9752
  Rotation = 0
  ScaleType = 0
  ShapeScale = 1
  SourceView = -> ProjItem001
  Text = 7
  TextWrapLen = -1
  X = 105
  Y = -25.2241
FEATURE [TechDraw::DrawViewDimExtent] DimExtent
  AngleOverride = false
  Arbitrary = false
  ArbitraryTolerances = false
  BoxCorners = (2) [(-38.5,-84.9426,-1e-07),(38.5,84.9426,1e-07)]
  DirExtent = 1
  EqualTolerance = true
  ExtensionAngle = 0
  FormatSpec = %.2w
  FormatSpecOverTolerance = %+.2w
  FormatSpecUnderTolerance = %+.2w
  Inverted = false
  LineAngle = 0
  LockPosition = false
  MeasureType = 1
  OverTolerance = 0
  References2D = -> [View001]
  Rotation = 0
  ScaleType = 0
  Source = -> [View001]
  TheoreticalExact = false
  Type = 2
  UnderTolerance = 0
  X = -95.2624
  Y = -0.005061
FEATURE [TechDraw::DrawViewAnnotation] Annotation
  Font = osifont
  LineSpace = 100
  LockPosition = false
  MaxWidth = -1
  Rotation = 0
  ScaleType = 0
  Text = Not all parts are shown
  TextSize = 5
  TextStyle = 0
  X = 417.461
  Y = 140.759
FEATURE [TechDraw::DrawViewDimension] Dimension005
  AngleOverride = false
  Arbitrary = false
  ArbitraryTolerances = false
  BoxCorners = (2) [(-42.3435,-79.4375,-1e-07),(42.3435,79.4375,1e-07)]
  EqualTolerance = true
  ExtensionAngle = 0
  FormatSpec = %.2w
  FormatSpecOverTolerance = %+.2w
  FormatSpecUnderTolerance = %+.2w
  Inverted = false
  LineAngle = 0
  LockPosition = false
  MeasureType = 1
  OverTolerance = 0
  References2D = -> [SectionView001]
  Rotation = 0
  ScaleType = 0
  TheoreticalExact = false
  Type = 2
  UnderTolerance = 0
  X = 55.6125
  Y = -72.175
FEATURE [TechDraw::DrawPage] Page
  KeepUpdated = true
  NextBalloonIndex = 34
  ProjectionType = 0
  Template = -> Template
  Views = -> [View,ProjGroup,SectionView,SectionView001,Sheet,Balloon,Balloon001,Balloon002,Balloon003,Balloon004,Balloon005,Balloon006,Balloon007,Balloon008,Balloon009,Annotation001,Balloon010,Balloon011,Balloon012,Balloon013,Balloon014,Balloon015,Balloon016,Dimension,Dimension001,Dimension002,Balloon017,Balloon018,Balloon019,Balloon020,Balloon021,Balloon022,Balloon023,Balloon024,Dimension003,Dimension004,+8 more]
FEATURE [TechDraw::DrawSVGTemplate] Template001
  Height = 210
  Orientation = 1
  Template = C:/Program Files/FreeCAD 1.0/data/Mod/TechDraw/Templates/Default_Template_A4_Landscape.svg
  Width = 297
FEATURE [TechDraw::DrawProjGroupItem] View002
  CoarseView = false
  Direction = (-0.57735,0.57735,-0.57735)
  Focus = 100
  HardHidden = false
  IsoCount = 0
  IsoHidden = false
  IsoVisible = false
  LockPosition = false
  Perspective = false
  Rotation = 0
  RotationVector = (1,0,0)
  Scale = 0.5
  ScaleType = 2
  ScrubCount = 1
  SeamHidden = false
  SeamVisible = false
  SmoothHidden = false
  SmoothVisible = true
  Source = -> [Assembly]
  Type = 0
  X = 148.5
  XDirection = (-0.707106,0,0.707106)
  Y = 105
FEATURE [TechDraw::DrawPage] Page001
  KeepUpdated = true
  NextBalloonIndex = 1
  ProjectionType = 0
  Template = -> Template001
  Views = -> [View002]
note: 4 file-system paths scrubbed to <path> (originals preserved in the JSON sidecar)
